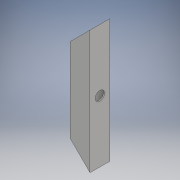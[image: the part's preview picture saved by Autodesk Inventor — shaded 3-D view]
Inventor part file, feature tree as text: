
AUTODESK INVENTOR PART (.ipt)
format: ipt  version: 2018 (Build 220112000, 112)  size: 114,688 bytes
history: native  units: mm
features: chamfer x2, sketch x2, other x1, extrude x1, hole x1
ambient origin geometry x8: Origin, YZ Plane, XZ Plane, XY Plane, X Axis, Y Axis, Z Axis, Center Point
bodies: Body1 (feature_tree)
feature tree (7):
  other  "ソリッド1"
  extrude  "押し出し1"  Depth=32.0mm
  chamfer  "面取り1"  Distance=32.0mm
  chamfer  "面取り2"  Distance=1.6mm
  hole  "穴1"  [1 undecoded]
  sketch  "スケッチ1"
  sketch  "スケッチ2"
note: 1 required parameter value undecoded (feature->parameter linkage not recoverable at this tier; creation-order binding heuristic only, values carry confidence <= 0.55)
